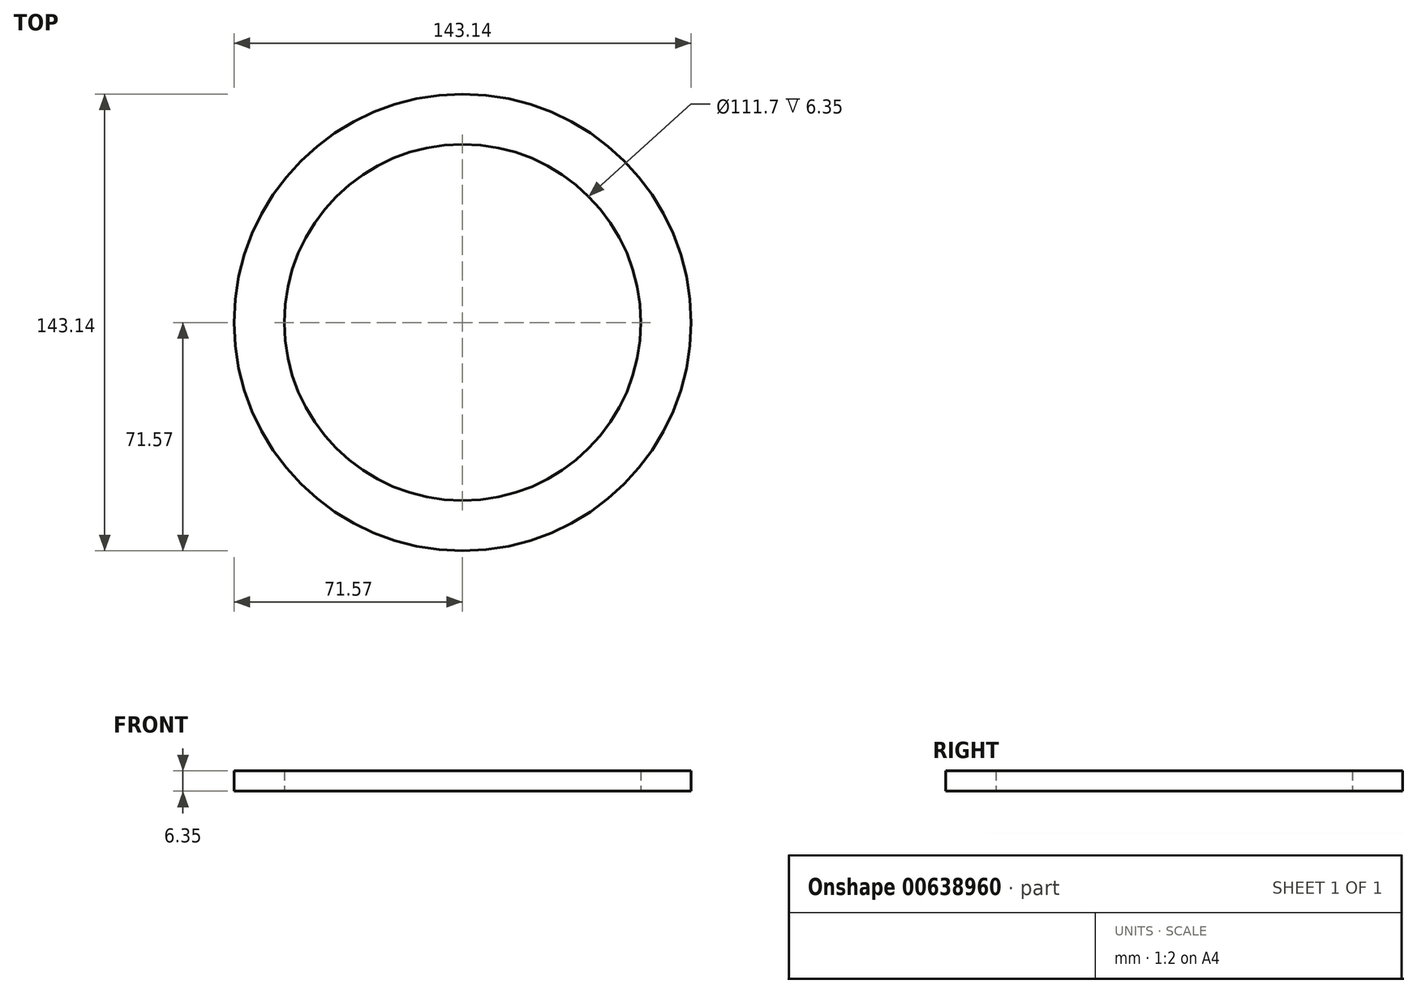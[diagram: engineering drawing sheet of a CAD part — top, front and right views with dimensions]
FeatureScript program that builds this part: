
annotation { "Feature Type Name" : "Feature", "Feature Type Description" : "" }
export const myFeature = defineFeature(function(context is Context, id is Id, definition is map)
    precondition{}
    {
        {
            var Q0;
            Q0=qCreatedBy(makeId("Top.planeOp"),FACE);
            var sketch = newSketch(context, id + "F0", { "sketchPlane" : qUnion([Q0])});
            skCircle(sketch, "E0", {"center": v(0, 0) * mm, "radius": 71.57 * mm});
            skSolve(sketch);
        }
        {
            var Q0;
            Q0 = qSketchRegion(id + "F0", true);
            var sketch = newSketch(context, id + "F1", { "sketchPlane" : qUnion([Q0])});
            skCircle(sketch, "E1", {"center": v(0, 0) * mm, "radius": 55.85 * mm});
            skSolve(sketch);
        }
        {
            var Q0;
            Q0=makeQuery(id+"F1.imprint","IMPRINT",FACE,{"disambiguationData":[TD([[makeQuery(id+"F1.imprint","IMPRINT",EDGE,{"derivedFrom":sQuery(id+"F1.wireOp",EDGE,"E1")}),-1.0]])]});
            extrude(context, id + "F2", {"entities" : qUnion([Q0]), "depth" : 6.35 * mm, "offsetDistance" : 25.4 * mm});
        }
    });
